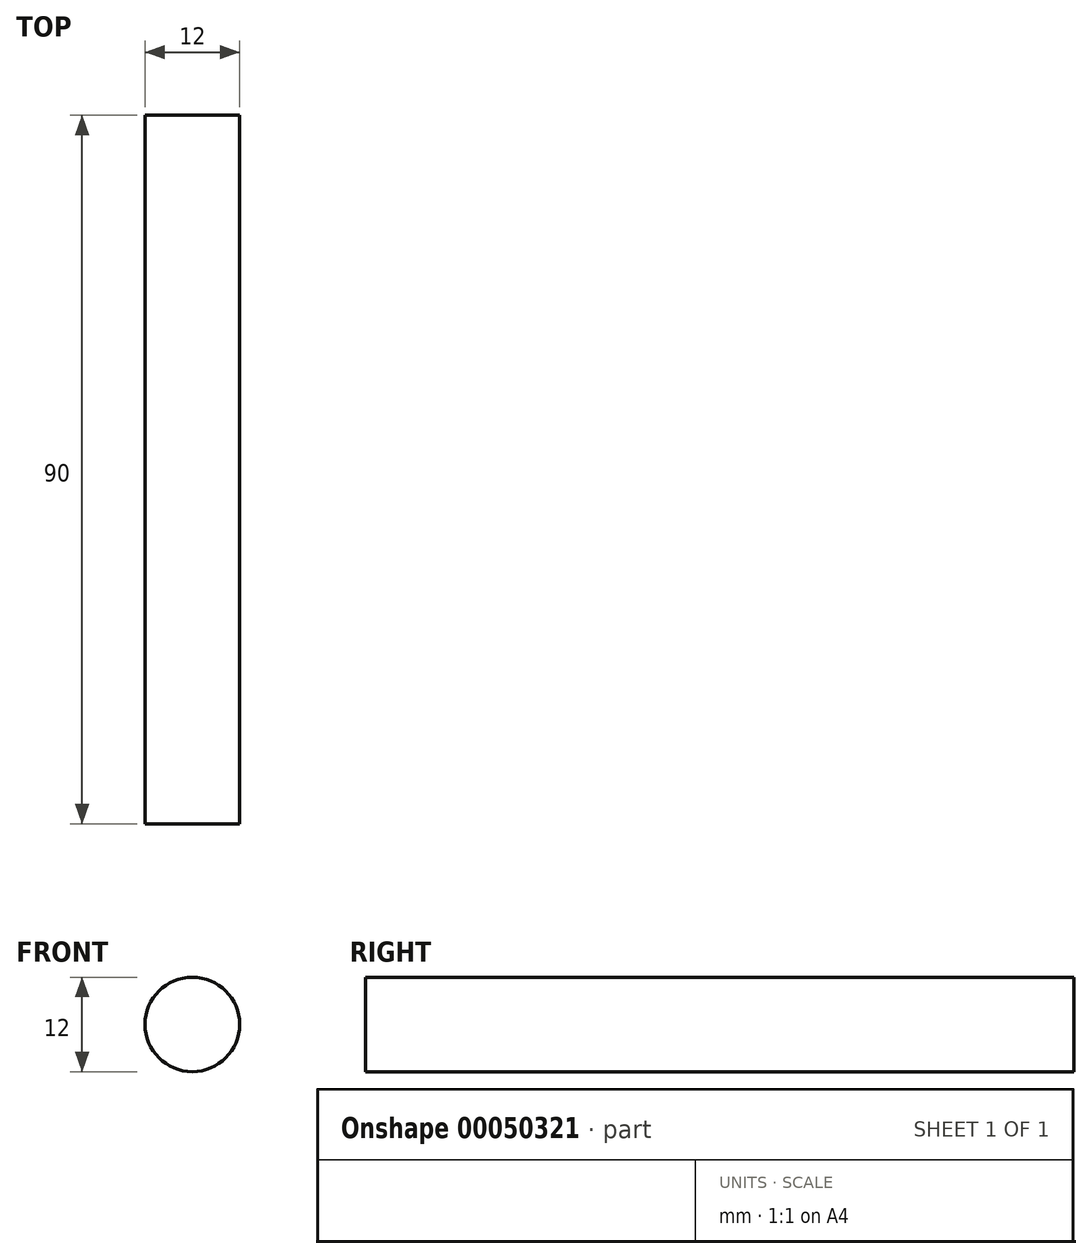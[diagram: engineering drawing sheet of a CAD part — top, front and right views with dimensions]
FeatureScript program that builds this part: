
annotation { "Feature Type Name" : "Feature", "Feature Type Description" : "" }
export const myFeature = defineFeature(function(context is Context, id is Id, definition is map)
    precondition{}
    {
        {
            var Q0;
            Q0=qCreatedBy(makeId("Front.planeOp"),FACE);
            var sketch = newSketch(context, id + "F0", { "sketchPlane" : qUnion([Q0])});
            skCircle(sketch, "E0", {"center": v(0, 0) * mm, "radius": 6 * mm});
            skSolve(sketch);
        }
        {
            var Q0;
            Q0 = qSketchRegion(id + "F0", true);
            extrude(context, id + "F1", {"entities" : qUnion([Q0]), "endBound" : BoundingType.SYMMETRIC, "depth" : (50 + 2 * 20) * mm});
        }
    });
